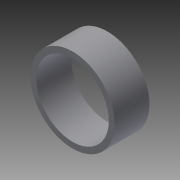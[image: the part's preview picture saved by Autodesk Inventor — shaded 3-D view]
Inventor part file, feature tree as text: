
AUTODESK INVENTOR PART (.ipt)
format: ipt  version: 2013 (Build 170138000, 138)  size: 80,384 bytes
history: native  units: in
note: dims shown in document units (in); Inventor stores cm internally (conversion verified against a paired STEP export)
features: extrude x1, sketch x1
ambient origin geometry x8: Origin, YZ Plane, XZ Plane, XY Plane, X Axis, Y Axis, Z Axis, Center Point
bodies: Solid1 (feature_tree)
feature tree (2):
  extrude  "Extrusion1"  Depth=1.25in
  sketch  "Sketch1"  dims[d0=1.45in d1=1.25in d2=0.6in d3=0.0in]
